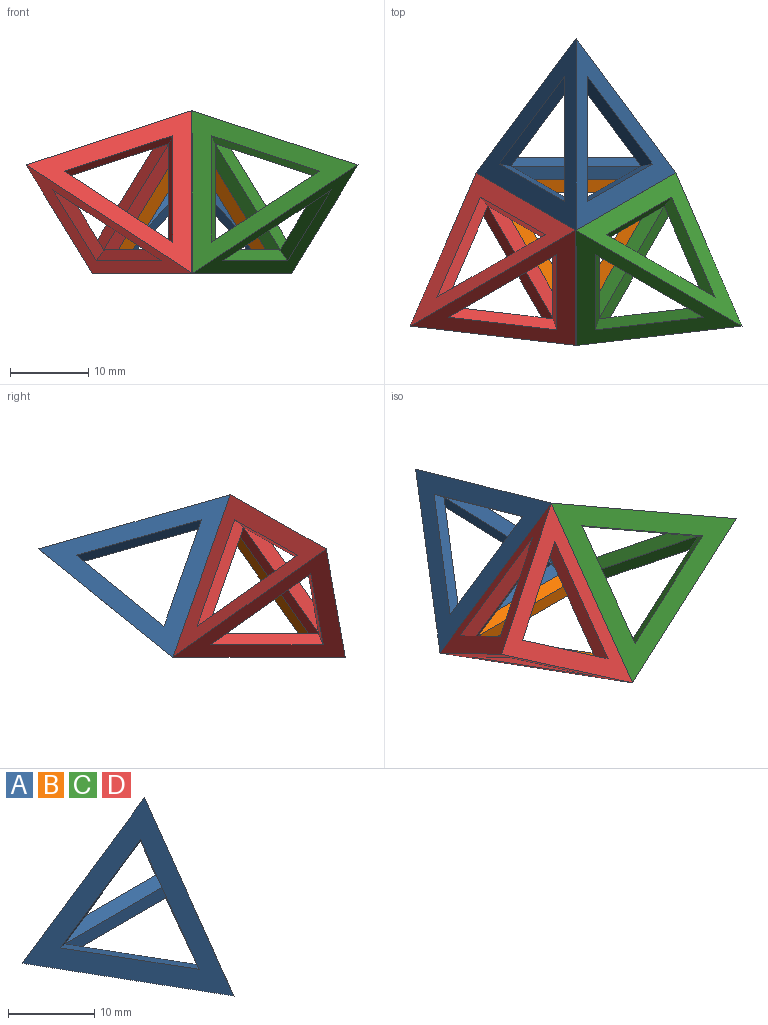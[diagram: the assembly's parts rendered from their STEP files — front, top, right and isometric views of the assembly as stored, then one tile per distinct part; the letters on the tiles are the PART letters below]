
ASSEMBLY  parts=4 mates=3
PART A: 52 faces, bbox 25.4x22x20.7 mm
  f0: plane 14.38x8.3mm, normal (0.87,0.5,0), area 29.8mm2, adj f1,f2,f11,f26,f28,f32,f47,f48
  f1: plane 14.38x8.3mm, normal (-0.87,0.5,0), area 29.8mm2, adj f0,f2,f9,f21,f28,f31,f39,f40
  f2: plane 16.6x1.8mm, normal (0,-1,0), area 29.8mm2, adj f0,f1,f5,f28,f33,f35,f49,f51
  f3: plane 14.15x8.3mm, normal (-0.87,0.17,-0.47), area 29.8mm2, adj f4,f5,f7,f16,f27,f29,f37,f42
  f4: plane 14.15x8.3mm, normal (0.87,0.17,-0.47), area 29.8mm2, adj f3,f5,f12,f23,f27,f30,f43,f45
  f5: plane 16.6x1.69mm, normal (0,-0.33,0.94), area 29.8mm2, adj f2,f3,f4,f27,f33,f34,f49,f50
  f6: plane 22x20.74mm, normal (0.82,-0.47,0.33), area 160mm2, adj f22,f27,f28,f40,f41,f42
  f7: plane 0.07x0.05mm, normal (0,0,-1), area 0mm2, adj f3,f8,f29,f42
  f8: plane 0.11x0.05mm, normal (-0.87,0.5,0), area 0mm2, adj f7,f29,f42
  f9: plane 0.07x0.05mm, normal (0,0.94,0.33), area 0mm2, adj f1,f10,f31,f40
  f10: plane 0.12x0.05mm, normal (-0.87,0.17,-0.47), area 0mm2, adj f9,f31,f40
  f11: plane 15.22x9.77mm, normal (0.29,0.17,0.94), area 29.8mm2, adj f0,f12,f13,f22,f25,f26,f46,f48
  f12: plane 14.15x9.77mm, normal (0.29,-0.83,-0.47), area 29.8mm2, adj f4,f11,f13,f22,f23,f24,f43,f44
  f13: plane 14.15x10.43mm, normal (-0.58,0.67,-0.47), area 29.8mm2, adj f11,f12,f15,f18,f22,f36,f38,f41
  f14: plane 0.1x0.08mm, normal (-0.87,0.17,-0.47), area 0mm2, adj f15,f36,f41
  f15: plane 0.07x0.06mm, normal (0,0.94,0.33), area 0mm2, adj f13,f14,f36,f41
  f16: plane 0.07x0.05mm, normal (-0.82,-0.47,0.33), area 0mm2, adj f3,f17,f37,f42
  f17: plane 0.09x0.08mm, normal (-0.58,0.67,-0.47), area 0mm2, adj f16,f37,f42
  f18: plane 0.08x0.06mm, normal (0,0,-1), area 0mm2, adj f13,f19,f38,f41
  f19: plane 0.11x0.05mm, normal (-0.87,0.5,0), area 0mm2, adj f18,f38,f41
  f20: plane 0.09x0.09mm, normal (-0.58,0.67,-0.47), area 0mm2, adj f21,f39,f40
  f21: plane 0.06x0.05mm, normal (-0.82,-0.47,0.33), area 0mm2, adj f1,f20,f39,f40
  f22: plane 22x20.74mm, normal (-0.82,-0.47,0.33), area 160mm2, adj f6,f11,f12,f13,f27,f28
  f23: plane 0.07x0.05mm, normal (0,0,-1), area 0mm2, adj f4,f12,f24,f30
  f24: plane 0.11x0.05mm, normal (0.87,0.5,0), area 0mm2, adj f12,f23,f30
  f25: plane 0.12x0.05mm, normal (0.87,0.17,-0.47), area 0mm2, adj f11,f26,f32
  f26: plane 0.07x0.05mm, normal (0,0.94,0.33), area 0mm2, adj f0,f11,f25,f32
  f27: plane 25.4x20.74mm, normal (0,0.94,0.33), area 160mm2, adj f3,f4,f5,f6,f22,f28
  f28: plane 25.4x22mm, normal (0,0,-1), area 160mm2, adj f0,f1,f2,f6,f22,f27
  f29: plane 0.11x0.06mm, normal (0,-1,0), area 0mm2, adj f3,f7,f8
  f30: plane 0.11x0.06mm, normal (0,-1,0), area 0mm2, adj f4,f23,f24
  f31: plane 0.1x0.06mm, normal (0,-0.33,0.94), area 0mm2, adj f1,f9,f10
  f32: plane 0.1x0.06mm, normal (0,-0.33,0.94), area 0mm2, adj f0,f25,f26
  f33: plane 0.05x0.05mm, normal (-0.82,-0.47,0.33), area 0mm2, adj f2,f5,f34,f35
  f34: plane 0.12x0.05mm, normal (0.29,-0.83,-0.47), area 0mm2, adj f5,f33,f35
  f35: plane 0.12x0.05mm, normal (0.29,0.17,0.94), area 0mm2, adj f2,f33,f34
  f36: plane 0.1x0.08mm, normal (0.87,0.17,-0.47), area 0mm2, adj f13,f14,f15
  f37: plane 0.09x0.08mm, normal (0.29,-0.83,-0.47), area 0mm2, adj f3,f16,f17
  f38: plane 0.11x0.05mm, normal (0.87,0.5,0), area 0mm2, adj f13,f18,f19
  f39: plane 0.1x0.09mm, normal (0.29,0.17,0.94), area 0mm2, adj f1,f20,f21
  f40: plane 15.22x9.77mm, normal (-0.29,0.17,0.94), area 29.8mm2, adj f1,f6,f9,f10,f20,f21,f41,f42
  f41: plane 14.15x10.43mm, normal (0.58,0.67,-0.47), area 29.8mm2, adj f6,f13,f14,f15,f18,f19,f40,f42
  f42: plane 14.15x9.77mm, normal (-0.29,-0.83,-0.47), area 29.8mm2, adj f3,f6,f7,f8,f16,f17,f40,f41
  f43: plane 0.07x0.05mm, normal (0.82,-0.47,0.33), area 0mm2, adj f4,f12,f44,f45
  f44: plane 0.09x0.08mm, normal (0.58,0.67,-0.47), area 0mm2, adj f12,f43,f45
  f45: plane 0.09x0.08mm, normal (-0.29,-0.83,-0.47), area 0mm2, adj f4,f43,f44
  f46: plane 0.09x0.09mm, normal (0.58,0.67,-0.47), area 0mm2, adj f11,f47,f48
  f47: plane 0.1x0.09mm, normal (-0.29,0.17,0.94), area 0mm2, adj f0,f46,f48
  f48: plane 0.06x0.05mm, normal (0.82,-0.47,0.33), area 0mm2, adj f0,f11,f46,f47
  f49: plane 0.05x0.05mm, normal (0.82,-0.47,0.33), area 0mm2, adj f2,f5,f50,f51
  f50: plane 0.12x0.05mm, normal (-0.29,-0.83,-0.47), area 0mm2, adj f5,f49,f51
  f51: plane 0.12x0.05mm, normal (-0.29,0.17,0.94), area 0mm2, adj f2,f49,f50
PART B: same geometry as A
PART C: same geometry as A
PART D: same geometry as A
PLACE A rot(axis=(0.63,-0.73,-0.26),131.8deg) t=(-10.85,-43.47,-4.4)mm
PLACE B t=(-9.29,-54.62,-0.18)mm fixed
PLACE C rot(axis=(-0.58,-0.67,0.47),180deg) t=(-48.16,-8.92,16.85)mm
PLACE D rot(axis=(0,0.58,0.82),70.5deg) t=(-13.83,-32.18,-16.05)mm
MATE fastened A.f6 <-> B.f27  axis (0,-0.94,-0.33) through (-30.99,-22.17,6.73)mm
MATE fastened D.f6 <-> B.f22  axis (0.82,0.47,-0.33) through (-35.23,-29.5,6.73)mm
MATE fastened C.f6 <-> B.f6  axis (-0.82,0.47,-0.33) through (-26.76,-29.5,6.73)mm
